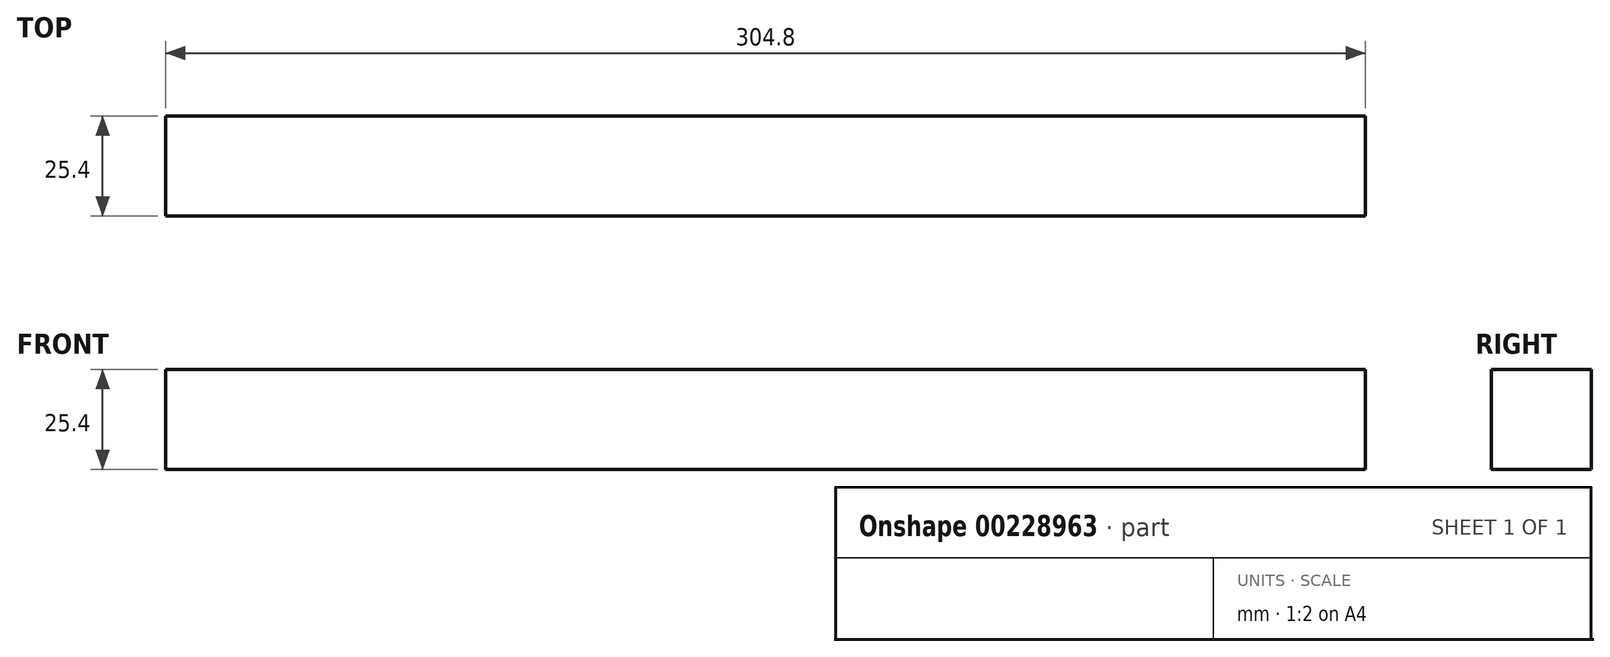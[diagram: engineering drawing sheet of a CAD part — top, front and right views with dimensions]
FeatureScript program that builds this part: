
annotation { "Feature Type Name" : "Feature", "Feature Type Description" : "" }
export const myFeature = defineFeature(function(context is Context, id is Id, definition is map)
    precondition{}
    {
        {
            var Q0;
            Q0=qCreatedBy(makeId("Top.planeOp"),FACE);
            var sketch = newSketch(context, id + "F0", { "sketchPlane" : qUnion([Q0])});
            skLineSegment(sketch, "E0.bottom", {"start": v(0, 0) * mm, "end": v(304.8, 0) * mm});
            skLineSegment(sketch, "E0.top", {"start": v(0, 25.4) * mm, "end": v(304.8, 25.4) * mm});
            skLineSegment(sketch, "E0.left", {"start": v(0, 0) * mm, "end": v(0, 25.4) * mm});
            skLineSegment(sketch, "E0.right", {"start": v(304.8, 0) * mm, "end": v(304.8, 25.4) * mm});
            skSolve(sketch);
        }
        {
            var Q0;
            Q0 = qSketchRegion(id + "F0", true);
            extrude(context, id + "F1", {"entities" : qUnion([Q0]), "depth" : 25.4 * mm});
        }
    });
